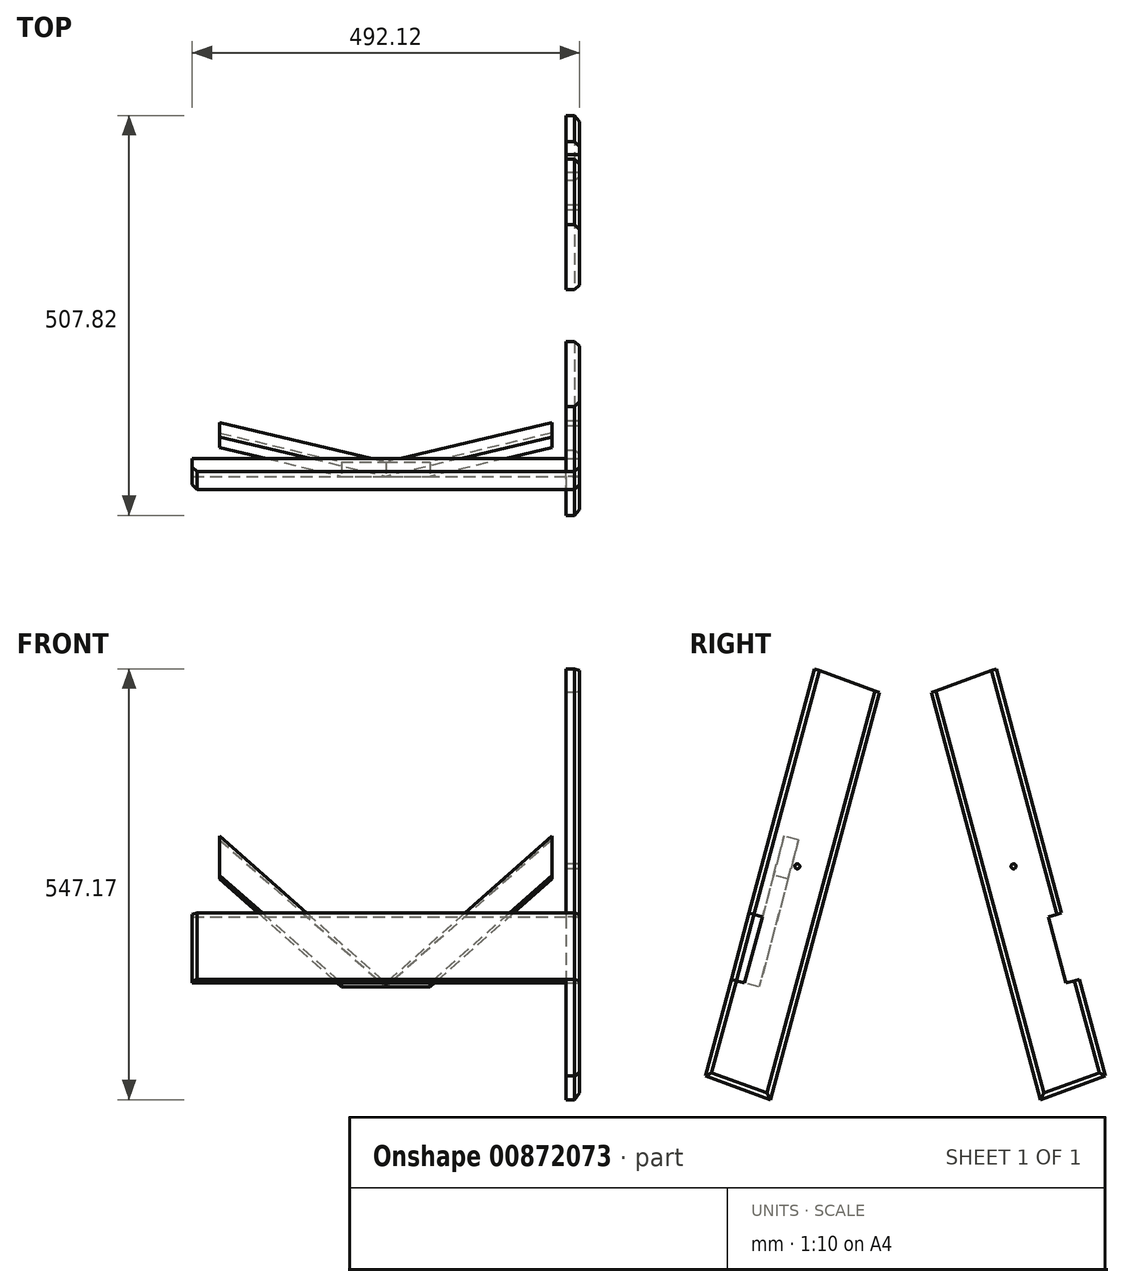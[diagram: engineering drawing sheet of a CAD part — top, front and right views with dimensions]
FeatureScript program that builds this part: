
annotation { "Feature Type Name" : "Feature", "Feature Type Description" : "" }
export const myFeature = defineFeature(function(context is Context, id is Id, definition is map)
    precondition{}
    {
        {
            var Q0;
            Q0=qCreatedBy(makeId("Right.planeOp"),FACE);
            var sketch = newSketch(context, id + "F0", { "sketchPlane" : qUnion([Q0])});
            skCircle(sketch, "E0", {"center": v(0, 0) * mm, "radius": 3.17 * mm, "construction": true});
            skCircle(sketch, "E1", {"center": v(0, 0) * mm, "radius": 43.66 * mm, "construction": true});
            skLineSegment(sketch, "E2", {"start": v(0, 0) * mm, "end": v(89.25, -32.49) * mm, "construction": true});
            skLineSegment(sketch, "E3", {"start": v(-42.17, 11.3) * mm, "end": v(42.17, -11.3) * mm, "construction": true});
            skLineSegment(sketch, "E4", {"start": v(22, 250.8) * mm, "end": v(-61.1, -59.39) * mm});
            skLineSegment(sketch, "E5", {"start": v(104.36, 220.82) * mm, "end": v(-34.22, -296.38) * mm});
            skLineSegment(sketch, "E6", {"start": v(22, 250.8) * mm, "end": v(104.36, 220.82) * mm});
            skLineSegment(sketch, "E7", {"start": v(-116.58, -266.4) * mm, "end": v(-34.22, -296.38) * mm});
            skCircle(sketch, "E8", {"center": v(0, 0) * mm, "radius": 3.13 * mm});
            skLineSegment(sketch, "E9", {"start": v(137.33, 282.03) * mm, "end": v(137.33, -341.7) * mm, "construction": true});
            skCircle(sketch, "E10.MirrorC", {"center": v(274.67, 0) * mm, "radius": 3.13 * mm});
            skCircle(sketch, "E11.MirrorC", {"center": v(274.67, 0) * mm, "radius": 3.17 * mm, "construction": true});
            skCircle(sketch, "E12.MirrorC", {"center": v(274.67, 0) * mm, "radius": 43.66 * mm, "construction": true});
            skLineSegment(sketch, "E13.MirrorCS", {"start": v(274.67, 0) * mm, "end": v(185.41, -32.49) * mm, "construction": true});
            skLineSegment(sketch, "E14.MirrorCS", {"start": v(316.83, 11.3) * mm, "end": v(232.5, -11.3) * mm, "construction": true});
            skLineSegment(sketch, "E15.MirrorCS", {"start": v(170.3, 220.82) * mm, "end": v(308.88, -296.38) * mm});
            skLineSegment(sketch, "E16.MirrorCS", {"start": v(252.66, 250.8) * mm, "end": v(170.3, 220.82) * mm});
            skLineSegment(sketch, "E17.MirrorCS", {"start": v(391.24, -266.4) * mm, "end": v(308.88, -296.38) * mm});
            skLineSegment(sketch, "E18", {"start": v(-61.1, -59.39) * mm, "end": v(-44.24, -63.9) * mm});
            skLineSegment(sketch, "E19", {"start": v(-44.24, -63.9) * mm, "end": v(-66.84, -148.25) * mm});
            skLineSegment(sketch, "E20", {"start": v(-66.84, -148.25) * mm, "end": v(-83.7, -143.73) * mm});
            skLineSegment(sketch, "E21.trimOffspring", {"start": v(-83.7, -143.73) * mm, "end": v(-116.58, -266.4) * mm});
            skLineSegment(sketch, "E22.MirrorCS", {"start": v(318.9, -63.9) * mm, "end": v(341.5, -148.25) * mm});
            skLineSegment(sketch, "E23.MirrorCS", {"start": v(335.77, -59.39) * mm, "end": v(318.9, -63.9) * mm});
            skLineSegment(sketch, "E24.MirrorCS", {"start": v(341.5, -148.25) * mm, "end": v(358.37, -143.73) * mm});
            skLineSegment(sketch, "E25.MirrorCS", {"start": v(252.66, 250.8) * mm, "end": v(335.77, -59.39) * mm});
            skLineSegment(sketch, "E26.MirrorCS", {"start": v(358.37, -143.73) * mm, "end": v(391.24, -266.4) * mm});
            skSolve(sketch);
        }
        {
            var Q0;
            Q0=qSketchRegion(id+"F0",true);
            var Q1;
            Q1=makeQuery(id+"F0.imprint","IMPRINT",FACE,{"disambiguationData":[TD([[makeQuery(id+"F0.imprint","IMPRINT",EDGE,{"derivedFrom":sQuery(id+"F0.wireOp",EDGE,"E4")}),1.0]])]});
            extrude(context, id + "F1", {"entities" : qUnion([Q0, Q1]), "depth" : 17.46 * mm});
        }
        {
            var Q0;
            Q0=makeQuery(id+"F1.opExtrude","CAP_FACE",FACE,{"disambiguationData":[OSD([sQuery(id+"F0.wireOp",EDGE,"E4"),sQuery(id+"F0.wireOp",EDGE,"E5"),sQuery(id+"F0.wireOp",EDGE,"E6"),sQuery(id+"F0.wireOp",EDGE,"E7"),sQuery(id+"F0.wireOp",EDGE,"E8"),sQuery(id+"F0.wireOp",EDGE,"E18"),sQuery(id+"F0.wireOp",EDGE,"E19"),sQuery(id+"F0.wireOp",EDGE,"E20"),sQuery(id+"F0.wireOp",EDGE,"E21.trimOffspring")])],"isStart":false});
            var sketch = newSketch(context, id + "F2", { "sketchPlane" : qUnion([Q0])});
            skLineSegment(sketch, "E27", {"start": v(-44.24, -63.9) * mm, "end": v(-66.84, -148.25) * mm});
            skLineSegment(sketch, "E28", {"start": v(-66.84, -148.25) * mm, "end": v(-83.7, -143.73) * mm});
            skLineSegment(sketch, "E29", {"start": v(-83.7, -143.73) * mm, "end": v(-61.1, -59.39) * mm});
            skLineSegment(sketch, "E30", {"start": v(-61.1, -59.39) * mm, "end": v(-46.15, -63.4) * mm});
            skSolve(sketch);
        }
        {
            var Q0;
            Q0=qSketchRegion(id+"F2",true);
            var Q1;
            {var subQ1=sQuery(id+"F2.wireOp",EDGE,"E27");Q1=makeQuery(id+"F2.imprint","IMPRINT",FACE,{"disambiguationData":[TD([[makeQuery(id+"F2.imprint","IMPRINT",EDGE,{"derivedFrom":subQ1}),-1.0]])]});}
            extrude(context, id + "F3", {"entities" : qUnion([Q0, Q1]), "depth" : -492.12 * mm});
        }
        {
            var Q0;
            Q0=makeQuery(id+"F3.opExtrude","CAP_EDGE",EDGE,{"disambiguationData":[OSD([sQuery(id+"F2.wireOp",EDGE,"E29")])],"isStart":true});
            var Q1;
            Q1=makeQuery(id+"F1.opExtrude","CAP_EDGE",EDGE,{"disambiguationData":[OSD([sQuery(id+"F0.wireOp",EDGE,"E4")])],"isStart":false});
            var Q2;
            Q2=makeQuery(id+"F1.opExtrude","CAP_EDGE",EDGE,{"disambiguationData":[OSD([sQuery(id+"F0.wireOp",EDGE,"E5")])],"isStart":false});
            var Q3;
            Q3=makeQuery(id+"F1.opExtrude","CAP_EDGE",EDGE,{"disambiguationData":[OSD([sQuery(id+"F0.wireOp",EDGE,"E21.trimOffspring")])],"isStart":false});
            var Q4;
            Q4=makeQuery(id+"F1.opExtrude","CAP_EDGE",EDGE,{"disambiguationData":[OSD([sQuery(id+"F0.wireOp",EDGE,"E7")])],"isStart":false});
            var Q5;
            Q5=makeQuery(id+"F1.opExtrude","CAP_EDGE",EDGE,{"disambiguationData":[OSD([sQuery(id+"F0.wireOp",EDGE,"E15.MirrorCS")])],"isStart":false});
            var Q6;
            Q6=makeQuery(id+"F1.opExtrude","CAP_EDGE",EDGE,{"disambiguationData":[OSD([sQuery(id+"F0.wireOp",EDGE,"E25.MirrorCS")])],"isStart":false});
            var Q7;
            Q7=makeQuery(id+"F1.opExtrude","CAP_EDGE",EDGE,{"disambiguationData":[OSD([sQuery(id+"F0.wireOp",EDGE,"E26.MirrorCS")])],"isStart":false});
            var Q8;
            Q8=makeQuery(id+"F1.opExtrude","CAP_EDGE",EDGE,{"disambiguationData":[OSD([sQuery(id+"F0.wireOp",EDGE,"E17.MirrorCS")])],"isStart":false});
            var Q9;
            Q9=makeQuery(id+"F3.opExtrude","CAP_EDGE",EDGE,{"disambiguationData":[OSD([sQuery(id+"F2.wireOp",EDGE,"E29")])],"isStart":false});
            chamfer(context, id + "F4", {"entities" : qUnion([Q0, Q1, Q2, Q3, Q4, Q5, Q6, Q7, Q8, Q9]), "width" : 6.35 * mm, "tangentPropagation" : true});
        }
        {
            var Q0;
            Q0=makeQuery(id+"F3.opExtrude","SWEPT_FACE",FACE,{"disambiguationData":[OSD([sQuery(id+"F2.wireOp",EDGE,"E27")])]});
            var sketch = newSketch(context, id + "F5", { "sketchPlane" : qUnion([Q0])});
            skLineSegment(sketch, "E31.MirrorCS", {"start": v(17.46, -18.7) * mm, "end": v(172.2, -160.5) * mm});
            skLineSegment(sketch, "E32.MirrorCS", {"start": v(172.2, -160.5) * mm, "end": v(228.6, -160.5) * mm});
            skLineSegment(sketch, "E33", {"start": v(17.46, -18.7) * mm, "end": v(17.46, -18.7) * mm});
            skLineSegment(sketch, "E34", {"start": v(17.46, 32.98) * mm, "end": v(228.6, -160.5) * mm});
            skLineSegment(sketch, "E35.bottom", {"start": v(17.46, 32.98) * mm, "end": v(439.74, 32.98) * mm, "construction": true});
            skLineSegment(sketch, "E35.right", {"start": v(439.74, 32.98) * mm, "end": v(439.74, -160.5) * mm, "construction": true});
            skLineSegment(sketch, "E36.bottom", {"start": v(439.74, 32.98) * mm, "end": v(474.66, 32.98) * mm, "construction": true});
            skLineSegment(sketch, "E36.top", {"start": v(439.74, -160.5) * mm, "end": v(474.66, -160.5) * mm, "construction": true});
            skLineSegment(sketch, "E36.right", {"start": v(474.66, 32.98) * mm, "end": v(474.66, -160.5) * mm, "construction": true});
            skLineSegment(sketch, "E37.bottom", {"start": v(17.46, 32.98) * mm, "end": v(-17.46, 32.98) * mm, "construction": true});
            skLineSegment(sketch, "E37.top", {"start": v(17.46, -160.5) * mm, "end": v(-17.46, -160.5) * mm, "construction": true});
            skLineSegment(sketch, "E37.right", {"start": v(-17.46, 32.98) * mm, "end": v(-17.46, -160.5) * mm, "construction": true});
            skLineSegment(sketch, "E38", {"start": v(17.46, -160.5) * mm, "end": v(172.2, -160.5) * mm, "construction": true});
            skLineSegment(sketch, "E39", {"start": v(228.6, 32.98) * mm, "end": v(228.6, -160.5) * mm, "construction": true});
            skLineSegment(sketch, "E40", {"start": v(228.6, -160.5) * mm, "end": v(439.74, -160.5) * mm, "construction": true});
            skLineSegment(sketch, "E41", {"start": v(17.46, -18.7) * mm, "end": v(17.46, 32.98) * mm});
            skLineSegment(sketch, "E42", {"start": v(17.46, -18.7) * mm, "end": v(17.46, -160.5) * mm, "construction": true});
            skLineSegment(sketch, "E43.MirrorCS", {"start": v(439.74, 32.98) * mm, "end": v(228.6, -160.5) * mm});
            skLineSegment(sketch, "E44.MirrorCS", {"start": v(439.74, -18.7) * mm, "end": v(439.74, 32.98) * mm});
            skLineSegment(sketch, "E45.MirrorCS", {"start": v(439.74, -18.7) * mm, "end": v(285, -160.5) * mm});
            skLineSegment(sketch, "E46.MirrorCS", {"start": v(285, -160.5) * mm, "end": v(228.6, -160.5) * mm});
            skSolve(sketch);
        }
        {
            var Q0;
            Q0=qSketchRegion(id+"F5",true);
            extrude(context, id + "F6", {"entities" : qUnion([Q0]), "depth" : 19.05 * mm});
        }
    });
